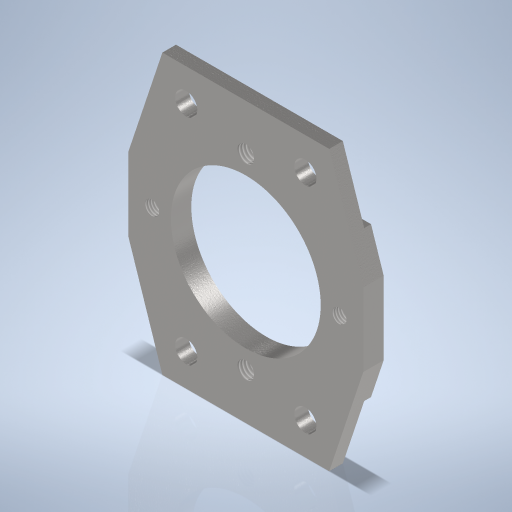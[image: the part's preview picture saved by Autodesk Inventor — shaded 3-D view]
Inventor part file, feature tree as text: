
AUTODESK INVENTOR PART (.ipt)
format: ipt  version: 2024 (Build 280153000, 153)  size: 348,160 bytes
history: native  units: mm
features: sketch x6, extrude x3, hole x3, plane x1
ambient origin geometry x8: Origin, YZ Plane, XZ Plane, XY Plane, X Axis, Y Axis, Z Axis, Center Point
bodies: Volumenkörper1 (feature_tree)
feature tree (13):
  extrude  "Extrusion1"  Depth=69.0mm
  extrude  "Extrusion2"  Depth=82.0mm
  extrude  "Extrusion3"  Depth=3.193953mm
  hole  "Bohrung1"  [1 undecoded]
  hole  "Bohrung2"  [1 undecoded]
  hole  "Bohrung3"  [1 undecoded]
  plane  "Arbeitsebene1"
  sketch  "Skizze1"  dims[d0=69.0mm d1=3.193953mm]
  sketch  "Skizze2"  dims[d2=49.0mm d4=82.0mm]
  sketch  "Skizze3"  dims[d5=3.193953mm d6=3.193953mm]
  sketch  "Skizze4"  dims[d7=3.193953mm d8=4.0mm d9=0.0mm]
  sketch  "Skizze5"  dims[d10=44.0mm d11=2.0mm d12=0.0mm]
  sketch  "Skizze6"  dims[d13=44.0mm d14=2.0mm d15=0.0mm d16=55.0mm d17=4.917mm d18=12.0mm d19=4.0mm d20=2.0mm d21=90.0deg d22=8.0mm d23=20.594885mm d24=6.5mm d25=10.0mm d26=4.0mm d27=2.0mm d28=90.0deg d29=8.0mm d30=20.594885mm d31=35.0mm d33=55.0mm d34=4.134mm d35=10.0mm d36=4.0mm d37=2.0mm d38=90.0deg d39=8.0mm d40=20.594885mm d41=-41.0mm d42=35.0mm d43=63.0mm]
note: 3 required parameter values undecoded (feature->parameter linkage not recoverable at this tier; creation-order binding heuristic only, values carry confidence <= 0.55)
